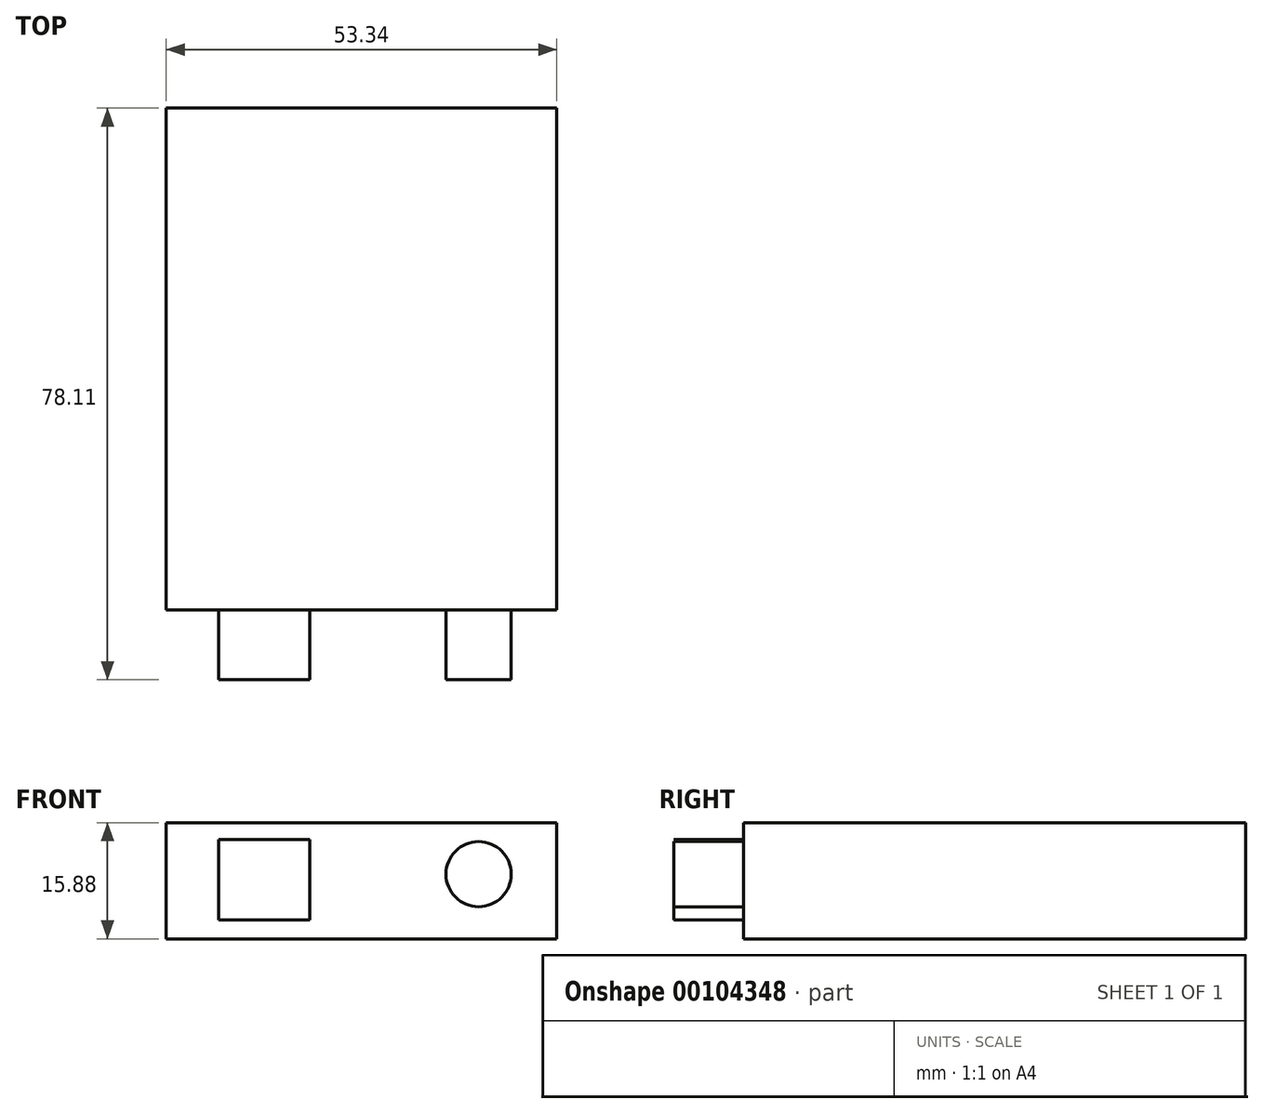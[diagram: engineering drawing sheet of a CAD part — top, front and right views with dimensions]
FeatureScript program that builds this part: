
annotation { "Feature Type Name" : "Feature", "Feature Type Description" : "" }
export const myFeature = defineFeature(function(context is Context, id is Id, definition is map)
    precondition{}
    {
        {
            var Q0;
            Q0=qCreatedBy(makeId("Top.planeOp"),FACE);
            var sketch = newSketch(context, id + "F0", { "sketchPlane" : qUnion([Q0])});
            skLineSegment(sketch, "E0.bottom", {"start": v(0, 0) * mm, "end": v(53.34, 0) * mm});
            skLineSegment(sketch, "E0.top", {"start": v(0, 68.58) * mm, "end": v(53.34, 68.58) * mm});
            skLineSegment(sketch, "E0.left", {"start": v(0, 0) * mm, "end": v(0, 68.58) * mm});
            skLineSegment(sketch, "E0.right", {"start": v(53.34, 0) * mm, "end": v(53.34, 68.58) * mm});
            skSolve(sketch);
        }
        {
            var Q0;
            Q0 = qSketchRegion(id + "F0", true);
            extrude(context, id + "F1", {"entities" : qUnion([Q0]), "depth" : 15.88 * mm});
        }
        {
            var Q0;
            Q0=makeQuery(id+"F1.opExtrude","SWEPT_FACE",FACE,{"disambiguationData":[OSD([sQuery(id+"F0.wireOp",EDGE,"E0.bottom")])]});
            var sketch = newSketch(context, id + "F2", { "sketchPlane" : qUnion([Q0])});
            skLineSegment(sketch, "E1.bottom", {"start": v(7.16, 13.58) * mm, "end": v(19.6, 13.58) * mm});
            skLineSegment(sketch, "E1.top", {"start": v(7.16, 2.57) * mm, "end": v(19.6, 2.57) * mm});
            skLineSegment(sketch, "E1.left", {"start": v(7.16, 13.58) * mm, "end": v(7.16, 2.57) * mm});
            skLineSegment(sketch, "E1.right", {"start": v(19.6, 13.58) * mm, "end": v(19.6, 2.57) * mm});
            skCircle(sketch, "E2", {"center": v(42.67, 8.83) * mm, "radius": 4.45 * mm});
            skSolve(sketch);
        }
        {
            var Q0;
            Q0 = qSketchRegion(id + "F2", true);
            extrude(context, id + "F3", {"entities" : qUnion([Q0]), "operationType" : NewBodyOperationType.ADD, "depth" : 9.52 * mm});
        }
    });
